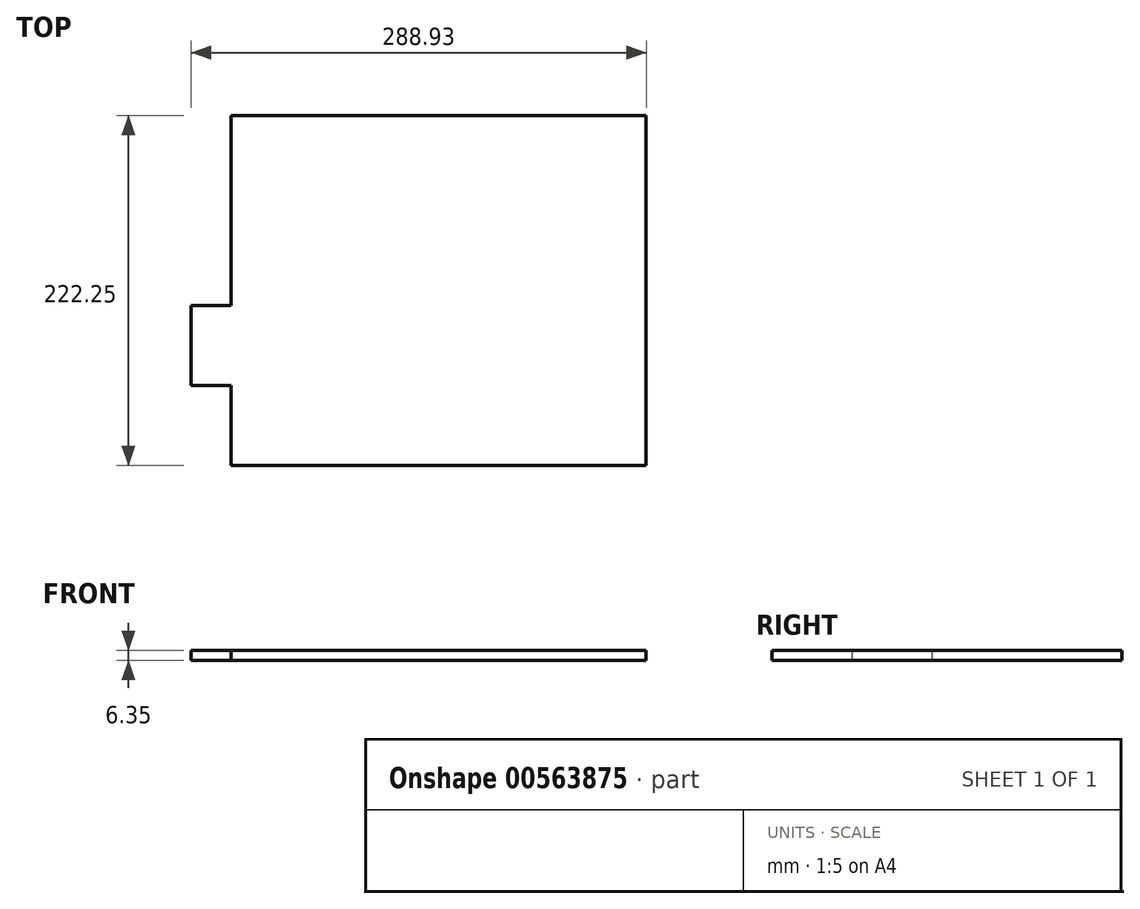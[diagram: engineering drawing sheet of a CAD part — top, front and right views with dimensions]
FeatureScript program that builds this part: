
annotation { "Feature Type Name" : "Feature", "Feature Type Description" : "" }
export const myFeature = defineFeature(function(context is Context, id is Id, definition is map)
    precondition{}
    {
        {
            var Q0;
            Q0=qCreatedBy(makeId("Top.planeOp"),FACE);
            var sketch = newSketch(context, id + "F0", { "sketchPlane" : qUnion([Q0])});
            skLineSegment(sketch, "E0", {"start": v(0, 0) * mm, "end": v(263.53, 0) * mm});
            skLineSegment(sketch, "E1", {"start": v(263.53, 0) * mm, "end": v(263.53, 222.25) * mm});
            skLineSegment(sketch, "E2", {"start": v(263.53, 222.25) * mm, "end": v(0, 222.25) * mm});
            skLineSegment(sketch, "E3", {"start": v(0, 222.25) * mm, "end": v(0, 101.6) * mm});
            skLineSegment(sketch, "E4", {"start": v(0, 101.6) * mm, "end": v(-25.4, 101.6) * mm});
            skLineSegment(sketch, "E5", {"start": v(-25.4, 101.6) * mm, "end": v(-25.4, 50.8) * mm});
            skLineSegment(sketch, "E6", {"start": v(-25.4, 50.8) * mm, "end": v(0, 50.8) * mm});
            skLineSegment(sketch, "E7", {"start": v(0, 50.8) * mm, "end": v(0, 0) * mm});
            skSolve(sketch);
        }
        {
            var Q0;
            Q0=makeQuery(id+"F0.imprint","IMPRINT",FACE,{"disambiguationData":[TD([[makeQuery(id+"F0.imprint","IMPRINT",EDGE,{"derivedFrom":sQuery(id+"F0.wireOp",EDGE,"E0")}),1.0]])]});
            extrude(context, id + "F1", {"entities" : qUnion([Q0]), "depth" : 6.35 * mm, "offsetDistance" : 25.4 * mm});
        }
    });
